# Revit family: ДВО-06 58 Вт 1195 DALI
name_source: partatom
category: Осветительные приборы
units: mm (PartAtom-declared; Revit-internal decimal feet)

## family parameters
Всегда вертикально = Да
Заголовок OmniClass = Luminaries for Internal Lighting
Источник света = Да
Номер OmniClass = 23.80.70.11
Общий = Нет
Основа = Потолок
При загрузке вырезать с полостями = Нет
Размер круглого соединителя = Использовать диаметр
Тип детали = Нормальный
Точка расчета площади = Нет

## types (6) — shared parameters
ADSK_Размер_Высота = 45 мм
ADSK_Размер_Длина = 1195 мм
ADSK_Размер_Ширина = 595 мм
URL = http://innolux.pro
Блок аварийного питания = нет
Бренд светодиодов = EDISON
Вес светильника = 5.72 кг
Время импульса пускового тока = 26 мс
Габаритная яркость = <5000 кд / м2
Гарантия = 7 лет
Диапазон рабочих температур = - 20 + 40°C
Диммирование = нет
Изготовитель = INNOLUX
Индекс цветопередачи = >80
Класс защиты от поражения током = I
Класс светораспределения по ГОСТ 54350-2011 = П
Климатическое исполнение = УХЛ 4
Кол-во светодиодов = 144
Количество в упаковке = 1
Количество модулей = 8
Коэффициент мощности = >0.95
>0.95
>0.95
Коэффициент пульсации = <5%
Материал корпуса = Металл, окрашенный, белый, матовый
Материал рассеивателя = Полистирол
Напряжение = 176-264 В
Объём упаковки = 1.21*0.61*0.055 м
Полная установленная мощность = 58 В·А
Потребляемый ток = 0
Пусковой ток = 17 А
Светофильтр = 16777215
Сила тока = 0.27 А
Смещение цветовой температуры при затухании лампы = <Нет>
Способ монтажа = Встраиваемый / Накладной
Срок службы = 80000
Степень защиты (IP) = 40
Тип кривой силы света по ГОСТ 54350-2011 = Д
Типоразмер светодиода = 2835
Угол наклона = 90.00°
Цвет корпуса = Белый
Частота сети = 50 / 60 Гц

## per-type parameters (varying)
| type | Артикул | Категория по ограничению яркости | Световой поток модуля | Тип рассеивателя | Файл фотометрической сетки | Эффективность светильника |
| ДВО-06-П-58-3К-IP40-DALI | 14683 | 3 | 968 | призма | INNOLUX 14 683 DVO-06-P-58-3K-IP40-DALI.ies | 134 |
| ДВО-06-П-58-4К-IP40-DALI | 14686 | 3 | 968 | призма | INNOLUX 14 686 DVO-06-P-58-4K-IP40-DALI.ies | 134 |
| ДВО-06-П-58-5К-IP40-DALI | 14689 | 3 | 968 | призма | INNOLUX 14 689 DVO-06-P-58-5K-IP40-DALI.ies | 134 |
| ДВО-06-О-58-3К-IP40-DALI | 14692 | 1 | 1047 | опал | INNOLUX 14 692 DVO-06-O-58-3K-IP40-DALI.ies | 122 |
| ДВО-06-О-58-4К-IP40-DALI | 14695 | 1 | 1047 | опал | INNOLUX 14 695 DVO-06-O-58-4K-IP40-DALI.ies | 122 |
| ДВО-06-О-58-5К-IP40-DALI | 14698 | 1 | 1047 | опал | INNOLUX 14 698 DVO-06-O-58-5K-IP40-DALI.ies | 122 |
